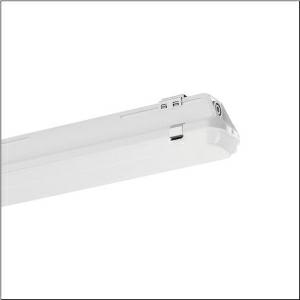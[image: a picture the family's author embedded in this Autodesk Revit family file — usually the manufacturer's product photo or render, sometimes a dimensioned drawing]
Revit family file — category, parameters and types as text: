
# Revit family: monsun_r__11_parking_51fg20dp440l007_7a89
name_source: partatom
category: Lighting Fixtures
units: mm (PartAtom-declared; Revit-internal decimal feet)

## family parameters
Cut with Voids When Loaded = No
Host = Face
Light Source = No
Part Type = Normal
Room Calculation Point = No
Round Connector Dimension = Use Diameter
Shared = No

## types (1)
- --- (1 x LED, 4840 lm, 28.1 W, 4000K)
    Apparent Load = 28 VA
    CIE Flux Codes = 45 75 93 94 100
    Color Rendering = 80
    Color Temperature = 4000K
    Default Elevation = 1800 mm
    Description = Monsun® 11 parking, damp-proof luminaire, chain hanger, primary optical cover: enclosure, of PC, light emission: direct distribution, primary light characteristic: symmetric, installation type: vertical mounting, horizontal mounting, surface-mounted, suspended mounting, LED, rated luminous flux: 4.840lm, luminous efficacy: 172lm/W, light colour: 840, colour temperature: 4000K, control gear: DALI 2, with terminal, 5-pole, max. 2.5mm², through-wiring: 7x 2.5mm², mains connection: 220..240V, AC, 50/60Hz, rated input power: 28W, housing, of glass-fibre reinforced polyester, uncoated, bright grey, incl. chain hanger, length: 1.590mm, width: 90mm, height: 88mm, clip for enclosure, of stainless steel (V2A), ceiling mounting element, of stainless steel (V2A), chain hanger, of stainless steel (V2A), protection rating (complete): IP66, insulation class (complete): insulation class I (protective earthing), certification: CE, ENEC, VDE, UKCA, protection symbol: D, impact resistance: IK08, permissible operating ambient temperature: -25..+40°C, standard: EN 50419, EN 60598-2-1, corresponds to IFS (International Featured Standards) requirements for safety and quality in the food industry, for indoor or canopied outdoor use, no direct snow, no direct sun, no direct rain, LABS conformity tested according to VDMA 24364:2018-05, contact your sales advisor before using the luminaires in applications with unclear chemical exposure, large temperature fluctuations or condensation-forming humidity, packaging unit: 1 piece
    Height = 89 mm
    Lamp = 1 x LED
    Lamp Light Flux = 4840 lm
    Lamp Power = 28.1 W
    Lamp count = 1
    Length = 1590 mm
    Luminous efficacy = 172 lm/W
    Manufacturer = Siteco
    ModVariant = No
    Model = 51FG20DP440L007
    Mounting Place = Ceiling
    Mounting Type = Surface mounted
    Number of Poles = 1
    OnlyDefault = Yes
    Power Factor = 1
    Product Name = Monsun® 11 parking
    Product group = damp-proof luminaire
    ProductGroupID = 301
    Protection Class = Protection class I
    Protection Degree = IP 66
    RLX_Detail_Level = 1
    RLX_Emergency_Light_Flux = 0 lm
    RLX_Emergency_Type = 0
    RLX_Emergency_Type_DB = No
    RlxData = <blob elided: 91833 chars, md5=aed59a05>
    Socket = socket
    Standby Power = 0 W
    System Light Flux = 4840 lm
    System Power = 28 W
    Type Comments = factory setting: luminous flux: 100 % | dim-lin: 254 | 193 mA
    Type Image = l_1349237.jpg
    URL = http://relux.com
    VarID = @adj_037577
    Voltage = 0 V
    Weight = 0.00 kg
    Width = 90 mm

## geometry (parser evidence)
native form markers: Blend x4, Sweep x13
no freeform markers — native parametric forms only
